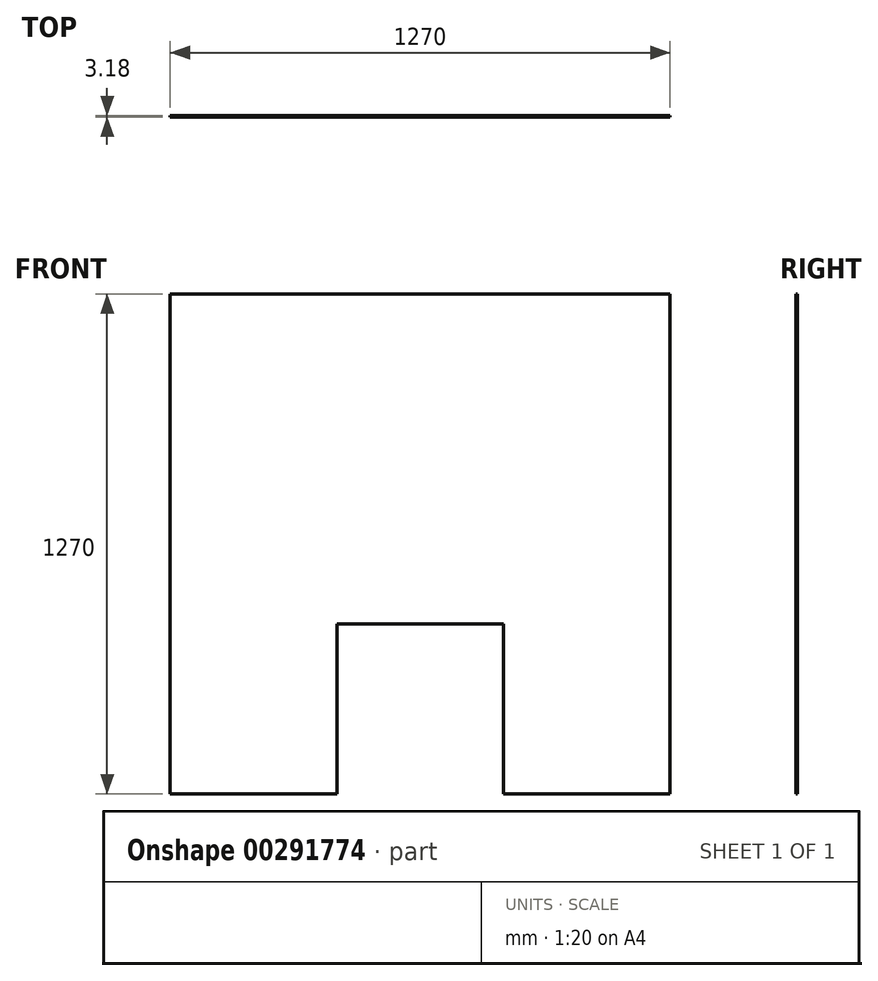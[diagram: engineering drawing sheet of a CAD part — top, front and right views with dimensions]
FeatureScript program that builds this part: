
annotation { "Feature Type Name" : "Feature", "Feature Type Description" : "" }
export const myFeature = defineFeature(function(context is Context, id is Id, definition is map)
    precondition{}
    {
        {
            var Q0;
            Q0=qCreatedBy(makeId("Front.planeOp"),FACE);
            var sketch = newSketch(context, id + "F0", { "sketchPlane" : qUnion([Q0])});
            skLineSegment(sketch, "E0.bottom", {"start": v(-635.49, 722.18) * mm, "end": v(634.51, 722.18) * mm});
            skLineSegment(sketch, "E0.top", {"start": v(-635.49, -547.82) * mm, "end": v(634.51, -547.82) * mm});
            skLineSegment(sketch, "E0.left", {"start": v(-635.49, 722.18) * mm, "end": v(-635.49, -547.82) * mm});
            skLineSegment(sketch, "E0.right", {"start": v(634.51, 722.18) * mm, "end": v(634.51, -547.82) * mm});
            skSolve(sketch);
        }
        {
            var Q0;
            Q0=makeQuery(id+"F0.imprint","IMPRINT",FACE,{"disambiguationData":[TD([[makeQuery(id+"F0.imprint","IMPRINT",EDGE,{"derivedFrom":sQuery(id+"F0.wireOp",EDGE,"E0.bottom")}),-1.0]])]});
            extrude(context, id + "F1", {"entities" : qUnion([Q0]), "endBound" : BoundingType.SYMMETRIC, "depth" : 3.17 * mm});
        }
        {
            var Q0;
            Q0=makeQuery(id+"F1.opExtrude","CAP_FACE",FACE,{"disambiguationData":[OSD([sQuery(id+"F0.wireOp",EDGE,"E0.bottom"),sQuery(id+"F0.wireOp",EDGE,"E0.top"),sQuery(id+"F0.wireOp",EDGE,"E0.left"),sQuery(id+"F0.wireOp",EDGE,"E0.right")])],"isStart":false});
            var sketch = newSketch(context, id + "F2", { "sketchPlane" : qUnion([Q0])});
            skLineSegment(sketch, "E1.bottom", {"start": v(-635.49, 722.18) * mm, "end": v(-635.49, 722.18) * mm});
            skLineSegment(sketch, "E1.top", {"start": v(-635.49, 645.98) * mm, "end": v(-635.49, 645.98) * mm});
            skLineSegment(sketch, "E1.left", {"start": v(-635.49, 722.18) * mm, "end": v(-635.49, 645.98) * mm, "construction": true});
            skLineSegment(sketch, "E1.right", {"start": v(-635.49, 722.18) * mm, "end": v(-635.49, 645.98) * mm, "construction": true});
            skLineSegment(sketch, "E2", {"start": v(-635.49, 722.18) * mm, "end": v(-597.39, 722.18) * mm, "construction": true});
            skLineSegment(sketch, "E3", {"start": v(-597.39, 722.18) * mm, "end": v(-597.39, -547.82) * mm, "construction": true});
            skLineSegment(sketch, "E4", {"start": v(-635.49, -547.82) * mm, "end": v(-212.07, -547.82) * mm, "construction": true});
            skLineSegment(sketch, "E5", {"start": v(634.51, -547.82) * mm, "end": v(211.1, -547.82) * mm, "construction": true});
            skLineSegment(sketch, "E6", {"start": v(-212.07, -547.82) * mm, "end": v(-212.07, -116.02) * mm, "construction": true});
            skLineSegment(sketch, "E7", {"start": v(211.1, -547.82) * mm, "end": v(211.1, -116.02) * mm, "construction": true});
            skLineSegment(sketch, "E8", {"start": v(-212.07, -116.02) * mm, "end": v(211.1, -116.02) * mm, "construction": true});
            skLineSegment(sketch, "E9", {"start": v(634.51, 722.18) * mm, "end": v(596.41, 722.18) * mm, "construction": true});
            skLineSegment(sketch, "E10", {"start": v(596.41, 722.18) * mm, "end": v(596.41, -547.82) * mm, "construction": true});
            skLineSegment(sketch, "E11", {"start": v(-635.49, 645.98) * mm, "end": v(634.51, 645.98) * mm, "construction": true});
            skLineSegment(sketch, "E12", {"start": v(-635.49, -547.82) * mm, "end": v(-635.49, -497.02) * mm, "construction": true});
            skLineSegment(sketch, "E13", {"start": v(-597.39, -497.02) * mm, "end": v(-559.29, -497.02) * mm, "construction": true});
            skLineSegment(sketch, "E14", {"start": v(-212.07, -497.02) * mm, "end": v(-250.17, -497.02) * mm, "construction": true});
            skLineSegment(sketch, "E15", {"start": v(211.1, -497.02) * mm, "end": v(249.2, -497.02) * mm, "construction": true});
            skLineSegment(sketch, "E16", {"start": v(596.41, -497.02) * mm, "end": v(558.31, -497.02) * mm, "construction": true});
            skLineSegment(sketch, "E17", {"start": v(211.1, -116.02) * mm, "end": v(211.1, -77.92) * mm, "construction": true});
            skLineSegment(sketch, "E18", {"start": v(-597.39, 645.98) * mm, "end": v(139.21, 645.98) * mm, "construction": true});
            skLineSegment(sketch, "E19", {"start": v(139.21, 645.98) * mm, "end": v(139.21, -77.92) * mm, "construction": true});
            skLineSegment(sketch, "E20", {"start": v(-597.39, -77.92) * mm, "end": v(139.21, -77.92) * mm, "construction": true});
            skLineSegment(sketch, "E21", {"start": v(211.1, -116.02) * mm, "end": v(249.2, -116.02) * mm, "construction": true});
            skLineSegment(sketch, "E22", {"start": v(-212.07, -116.02) * mm, "end": v(-250.17, -116.02) * mm, "construction": true});
            skLineSegment(sketch, "E23", {"start": v(211.1, 645.98) * mm, "end": v(596.41, 645.98) * mm, "construction": true});
            skLineSegment(sketch, "E24.bottom", {"start": v(-597.39, -116.02) * mm, "end": v(-250.17, -116.02) * mm, "construction": true});
            skLineSegment(sketch, "E24.top", {"start": v(-597.39, -243.02) * mm, "end": v(-250.17, -243.02) * mm, "construction": true});
            skLineSegment(sketch, "E24.left", {"start": v(-597.39, -116.02) * mm, "end": v(-597.39, -243.02) * mm, "construction": true});
            skLineSegment(sketch, "E24.right", {"start": v(-250.17, -116.02) * mm, "end": v(-250.17, -243.02) * mm, "construction": true});
            skLineSegment(sketch, "E25.bottom", {"start": v(249.2, 645.98) * mm, "end": v(596.41, 645.98) * mm, "construction": true});
            skLineSegment(sketch, "E25.top", {"start": v(249.2, -243.02) * mm, "end": v(596.41, -243.02) * mm, "construction": true});
            skLineSegment(sketch, "E25.left", {"start": v(249.2, 645.98) * mm, "end": v(249.2, -243.02) * mm, "construction": true});
            skLineSegment(sketch, "E25.right", {"start": v(596.41, 645.98) * mm, "end": v(596.41, -243.02) * mm, "construction": true});
            skLineSegment(sketch, "E26", {"start": v(-250.17, -243.02) * mm, "end": v(-250.17, -255.72) * mm, "construction": true});
            skLineSegment(sketch, "E27.bottom", {"start": v(-597.39, -255.72) * mm, "end": v(-250.17, -255.72) * mm, "construction": true});
            skLineSegment(sketch, "E27.top", {"start": v(-597.39, -382.72) * mm, "end": v(-250.17, -382.72) * mm, "construction": true});
            skLineSegment(sketch, "E27.left", {"start": v(-597.39, -255.72) * mm, "end": v(-597.39, -382.72) * mm, "construction": true});
            skLineSegment(sketch, "E27.right", {"start": v(-250.17, -255.72) * mm, "end": v(-250.17, -382.72) * mm, "construction": true});
            skLineSegment(sketch, "E28", {"start": v(-250.17, -382.72) * mm, "end": v(-250.17, -396.8) * mm});
            skLineSegment(sketch, "E29.bottom", {"start": v(-250.17, -396.8) * mm, "end": v(-597.39, -396.8) * mm, "construction": true});
            skLineSegment(sketch, "E29.top", {"start": v(-250.17, -523.8) * mm, "end": v(-597.39, -523.8) * mm, "construction": true});
            skLineSegment(sketch, "E29.left", {"start": v(-250.17, -396.8) * mm, "end": v(-250.17, -523.8) * mm, "construction": true});
            skLineSegment(sketch, "E29.right", {"start": v(-597.39, -396.8) * mm, "end": v(-597.39, -523.8) * mm, "construction": true});
            skLineSegment(sketch, "E30", {"start": v(-250.17, -523.8) * mm, "end": v(-250.17, -547.82) * mm, "construction": true});
            skLineSegment(sketch, "E31.bottom", {"start": v(249.2, -255.72) * mm, "end": v(596.41, -255.72) * mm});
            skLineSegment(sketch, "E31.top", {"start": v(249.2, -382.72) * mm, "end": v(596.41, -382.72) * mm});
            skLineSegment(sketch, "E31.left", {"start": v(249.2, -255.72) * mm, "end": v(249.2, -382.72) * mm});
            skLineSegment(sketch, "E31.right", {"start": v(596.41, -255.72) * mm, "end": v(596.41, -382.72) * mm});
            skLineSegment(sketch, "E32.bottom", {"start": v(249.2, -396.8) * mm, "end": v(596.41, -396.8) * mm});
            skLineSegment(sketch, "E32.top", {"start": v(249.2, -523.8) * mm, "end": v(596.41, -523.8) * mm});
            skLineSegment(sketch, "E32.left", {"start": v(249.2, -396.8) * mm, "end": v(249.2, -523.8) * mm});
            skLineSegment(sketch, "E32.right", {"start": v(596.41, -396.8) * mm, "end": v(596.41, -523.8) * mm});
            skLineSegment(sketch, "E33.bottom", {"start": v(-597.39, 645.98) * mm, "end": v(139.21, 645.98) * mm});
            skLineSegment(sketch, "E33.top", {"start": v(-597.39, -77.92) * mm, "end": v(139.21, -77.92) * mm});
            skLineSegment(sketch, "E33.left", {"start": v(-597.39, 645.98) * mm, "end": v(-597.39, -77.92) * mm});
            skLineSegment(sketch, "E33.right", {"start": v(139.21, 645.98) * mm, "end": v(139.21, -77.92) * mm});
            skLineSegment(sketch, "E34.bottom", {"start": v(249.2, 645.98) * mm, "end": v(596.41, 645.98) * mm});
            skLineSegment(sketch, "E34.top", {"start": v(249.2, -243.02) * mm, "end": v(596.41, -243.02) * mm});
            skLineSegment(sketch, "E34.left", {"start": v(249.2, 645.98) * mm, "end": v(249.2, -243.02) * mm});
            skLineSegment(sketch, "E34.right", {"start": v(596.41, 645.98) * mm, "end": v(596.41, -243.02) * mm});
            skLineSegment(sketch, "E35.bottom", {"start": v(-597.39, -116.02) * mm, "end": v(-250.17, -116.02) * mm});
            skLineSegment(sketch, "E35.top", {"start": v(-597.39, -243.02) * mm, "end": v(-250.17, -243.02) * mm});
            skLineSegment(sketch, "E35.left", {"start": v(-597.39, -116.02) * mm, "end": v(-597.39, -243.02) * mm});
            skLineSegment(sketch, "E35.right", {"start": v(-250.17, -116.02) * mm, "end": v(-250.17, -243.02) * mm});
            skLineSegment(sketch, "E36.bottom", {"start": v(-597.39, -255.72) * mm, "end": v(-250.17, -255.72) * mm});
            skLineSegment(sketch, "E36.top", {"start": v(-597.39, -382.72) * mm, "end": v(-250.17, -382.72) * mm});
            skLineSegment(sketch, "E36.left", {"start": v(-597.39, -255.72) * mm, "end": v(-597.39, -382.72) * mm});
            skLineSegment(sketch, "E36.right", {"start": v(-250.17, -255.72) * mm, "end": v(-250.17, -382.72) * mm});
            skLineSegment(sketch, "E37.bottom", {"start": v(-597.39, -396.8) * mm, "end": v(-250.17, -396.8) * mm});
            skLineSegment(sketch, "E37.top", {"start": v(-597.39, -523.8) * mm, "end": v(-250.17, -523.8) * mm});
            skLineSegment(sketch, "E37.left", {"start": v(-597.39, -396.8) * mm, "end": v(-597.39, -523.8) * mm});
            skLineSegment(sketch, "E37.right", {"start": v(-250.17, -396.8) * mm, "end": v(-250.17, -523.8) * mm});
            skLineSegment(sketch, "E38.bottom", {"start": v(-212.07, -116.02) * mm, "end": v(211.1, -116.02) * mm});
            skLineSegment(sketch, "E38.top", {"start": v(-212.07, -547.82) * mm, "end": v(211.1, -547.82) * mm});
            skLineSegment(sketch, "E38.left", {"start": v(-212.07, -116.02) * mm, "end": v(-212.07, -547.82) * mm});
            skLineSegment(sketch, "E38.right", {"start": v(211.1, -116.02) * mm, "end": v(211.1, -547.82) * mm});
            skSolve(sketch);
        }
        {
            var Q0;
            Q0=makeQuery(id+"F2.imprint","IMPRINT",FACE,{"disambiguationData":[TD([[makeQuery(id+"F2.imprint","IMPRINT",EDGE,{"derivedFrom":sQuery(id+"F2.wireOp",EDGE,"E38.bottom")}),-1.0]])]});
            extrude(context, id + "F3", {"entities" : qUnion([Q0]), "operationType" : NewBodyOperationType.REMOVE, "endBound" : BoundingType.THROUGH_ALL, "oppositeDirection" : true, "depth" : 25.4 * mm});
        }
    });
